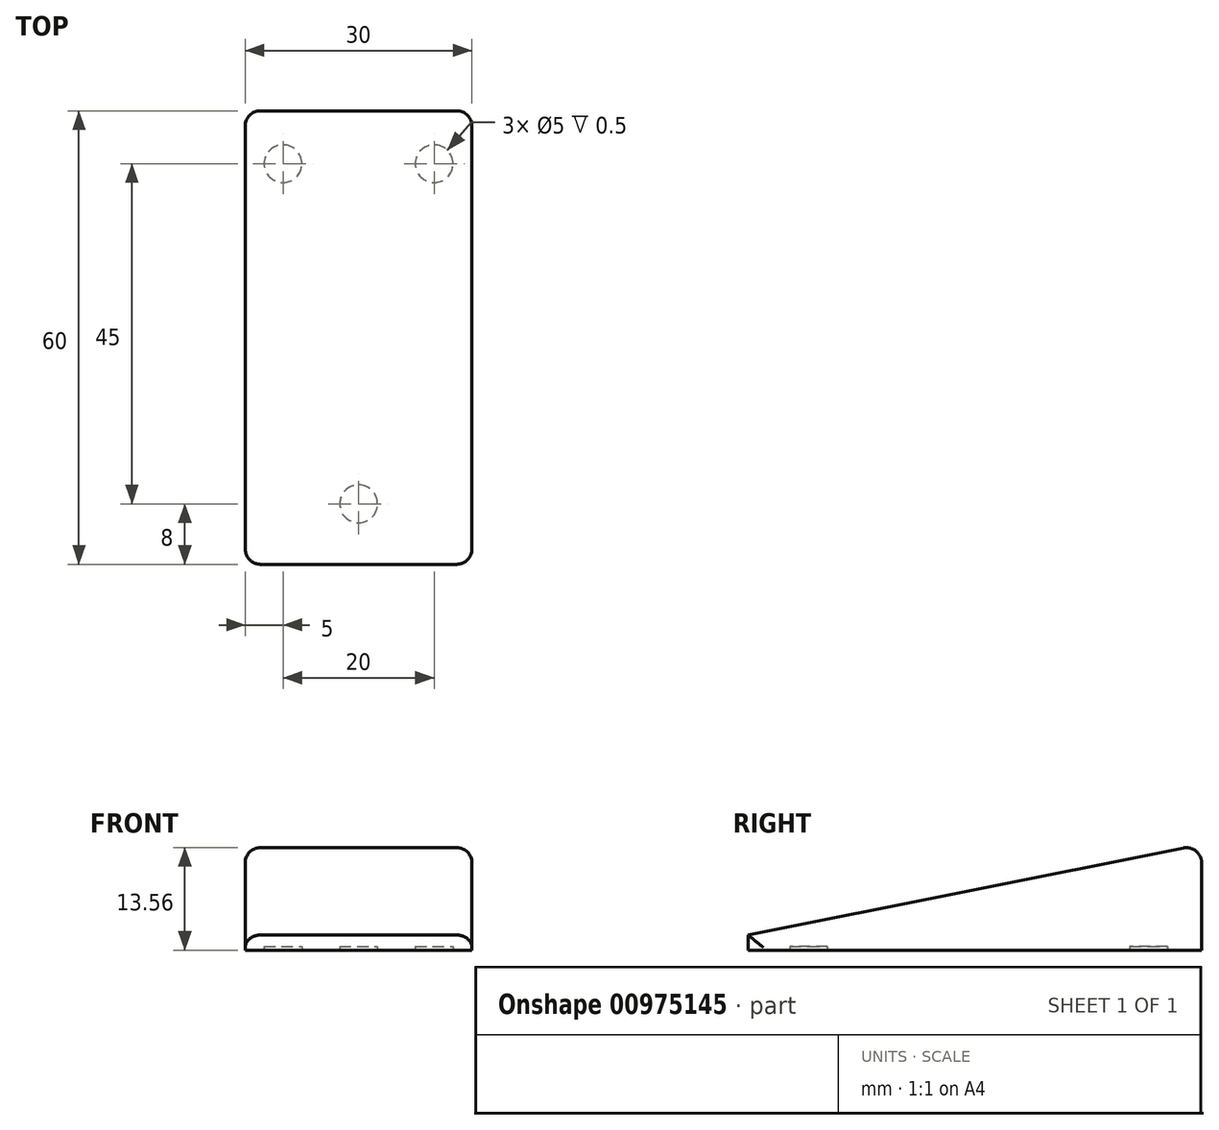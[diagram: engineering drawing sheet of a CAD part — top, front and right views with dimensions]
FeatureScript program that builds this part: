
annotation { "Feature Type Name" : "Feature", "Feature Type Description" : "" }
export const myFeature = defineFeature(function(context is Context, id is Id, definition is map)
    precondition{}
    {
        {
            var Q0;
            Q0=qCreatedBy(makeId("Right.planeOp"),FACE);
            var sketch = newSketch(context, id + "F0", { "sketchPlane" : qUnion([Q0])});
            skLineSegment(sketch, "E0", {"start": v(0, 14) * mm, "end": v(0, 0) * mm});
            skLineSegment(sketch, "E1", {"start": v(0, 0) * mm, "end": v(-60, 0) * mm});
            skLineSegment(sketch, "E2", {"start": v(-60, 0) * mm, "end": v(-60, 2) * mm});
            skLineSegment(sketch, "E3", {"start": v(-60, 2) * mm, "end": v(0, 14) * mm});
            skSolve(sketch);
        }
        {
            var Q0;
            Q0=makeQuery(id+"F0.imprint","IMPRINT",FACE,{"disambiguationData":[TD([[makeQuery(id+"F0.imprint","IMPRINT",EDGE,{"derivedFrom":sQuery(id+"F0.wireOp",EDGE,"E0")}),-1.0]])]});
            extrude(context, id + "F1", {"entities" : qUnion([Q0]), "endBound" : BoundingType.SYMMETRIC, "depth" : 30 * mm, "offsetDistance" : 25 * mm});
        }
        {
            var Q0;
            Q0=makeQuery(id+"F1.opExtrude","SWEPT_FACE",FACE,{"disambiguationData":[OSD([sQuery(id+"F0.wireOp",EDGE,"E1")])]});
            var sketch = newSketch(context, id + "F2", { "sketchPlane" : qUnion([Q0])});
            skCircle(sketch, "E4", {"center": v(0, 52) * mm, "radius": 2.5 * mm});
            skCircle(sketch, "E5", {"center": v(10, 7) * mm, "radius": 2.5 * mm});
            skCircle(sketch, "E6.MirrorC", {"center": v(-10, 7) * mm, "radius": 2.5 * mm});
            skSolve(sketch);
        }
        {
            var Q0;
            Q0 = qSketchRegion(id + "F2", true);
            extrude(context, id + "F3", {"entities" : qUnion([Q0]), "operationType" : NewBodyOperationType.REMOVE, "oppositeDirection" : true, "depth" : 0.5 * mm, "offsetDistance" : 25 * mm});
        }
        {
            var Q0;
            Q0=makeQuery(id+"F1.opExtrude","CAP_EDGE",EDGE,{"disambiguationData":[OSD([sQuery(id+"F0.wireOp",EDGE,"E3")])],"isStart":false});
            var Q1;
            Q1=makeQuery(id+"F1.opExtrude","CAP_EDGE",EDGE,{"disambiguationData":[OSD([sQuery(id+"F0.wireOp",EDGE,"E3")])],"isStart":true});
            var Q2;
            Q2=makeQuery(id+"F1.opExtrude","CAP_EDGE",EDGE,{"disambiguationData":[OSD([sQuery(id+"F0.wireOp",EDGE,"E0")])],"isStart":true});
            var Q3;
            Q3=makeQuery(id+"F1.opExtrude","SWEPT_EDGE",EDGE,{"disambiguationData":[OSD([sQuery(id+"F0.wireOp",EDGE,"E0"),sQuery(id+"F0.wireOp",EDGE,"E3")])]});
            var Q4;
            Q4=makeQuery(id+"F1.opExtrude","CAP_EDGE",EDGE,{"disambiguationData":[OSD([sQuery(id+"F0.wireOp",EDGE,"E0")])],"isStart":false});
            var Q5;
            Q5=makeQuery(id+"F1.opExtrude","CAP_EDGE",EDGE,{"disambiguationData":[OSD([sQuery(id+"F0.wireOp",EDGE,"E2")])],"isStart":true});
            var Q6;
            Q6=makeQuery(id+"F1.opExtrude","CAP_EDGE",EDGE,{"disambiguationData":[OSD([sQuery(id+"F0.wireOp",EDGE,"E2")])],"isStart":false});
            fillet(context, id + "F4", {"entities" : qUnion([Q0, Q1, Q2, Q3, Q4, Q5, Q6]), "radius" : 2 * mm, "tangentPropagation" : true, "allowEdgeOverflow" : false});
        }
    });
